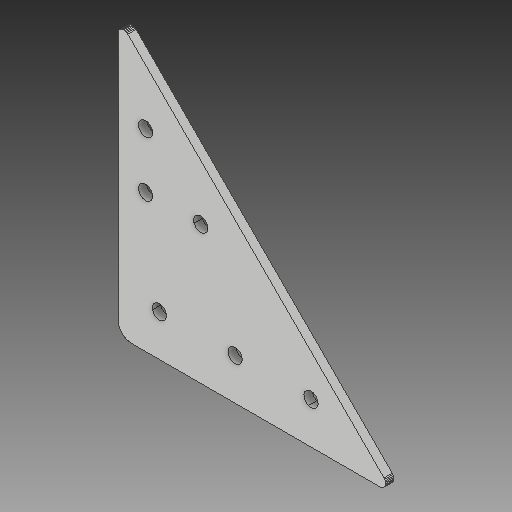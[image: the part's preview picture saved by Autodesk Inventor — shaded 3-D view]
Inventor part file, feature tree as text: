
AUTODESK INVENTOR PART (.ipt)
format: ipt  version: 2018 (Build 220112000, 112)  size: 209,920 bytes
history: native  units: mm
features: other x3, sketch x1
ambient origin geometry x8: Origin, YZ Plane, XZ Plane, XY Plane, X Axis, Y Axis, Z Axis, Center Point
bodies: Solid1 (feature_tree)
feature tree (4):
  other  "Side Brace_MIR.ipt"
  other  "Solid1::Side Brace_MIR.ipt"
  other  "TaggingFeature1"
  sketch  "Sketch1"  dims[d0=10.0mm]
